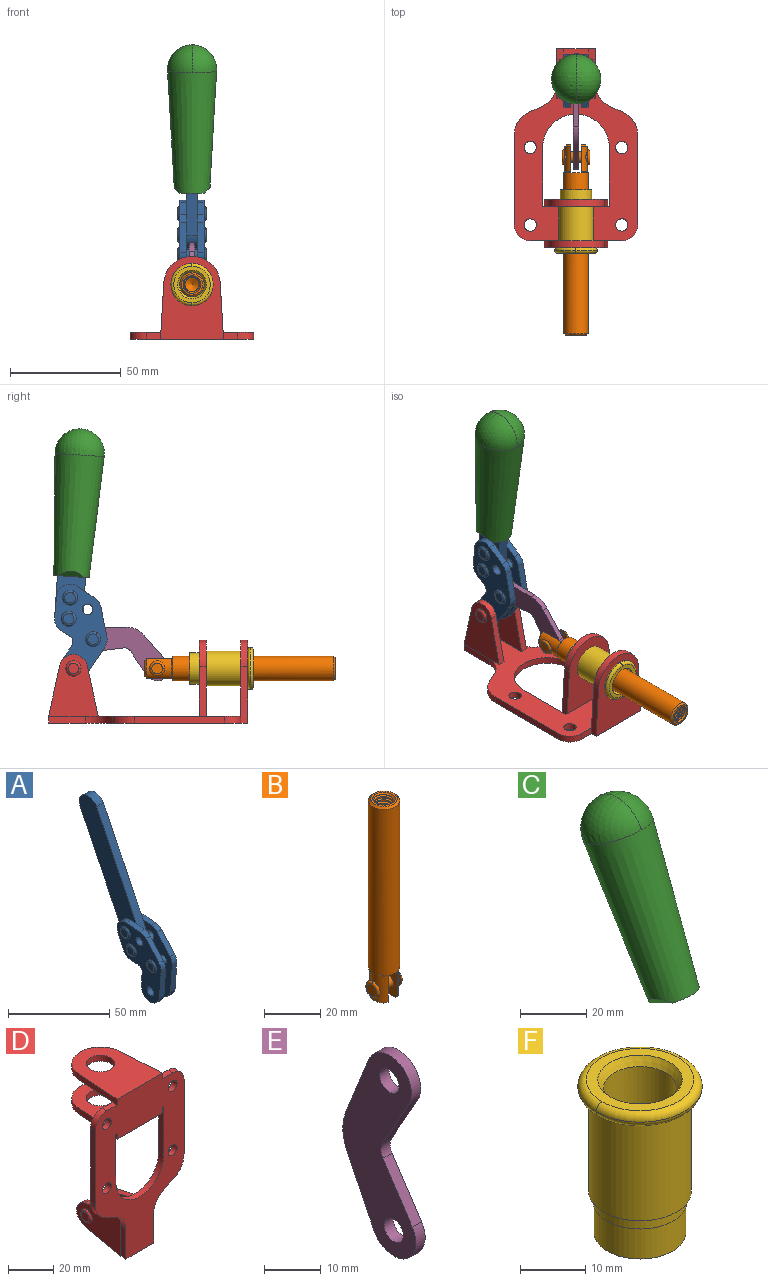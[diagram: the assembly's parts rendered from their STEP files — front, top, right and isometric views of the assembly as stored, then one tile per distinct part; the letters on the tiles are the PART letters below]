
ASSEMBLY  parts=6 mates=6
PART A: 59 faces, bbox 12.9x60.2x99.6 mm
  f0: torus R=2.39mm, axis (-1,0,0), area 14.9mm2, adj f20,f43,f51
  f1: torus R=2.39mm, axis (-1,0,0), area 14.9mm2, adj f19,f42,f51
  f2: torus R=2.39mm, axis (-1,0,0), area 14.9mm2, adj f18,f35,f51
  f3: torus R=2.39mm, axis (-1,0,0), area 14.9mm2, adj f14,f17,f23
  f4: torus R=2.39mm, axis (-1,0,0), area 14.9mm2, adj f13,f16,f23
  f5: torus R=2.39mm, axis (-1,0,0), area 14.9mm2, adj f12,f15,f23
  f6: cylinder r=2.39mm len=4.78mm, axis (1,0,0), area 46.5mm2, adj f48,f50,f51
  f7: cylinder r=2.39mm len=4.78mm, axis (1,0,0), area 46.5mm2, adj f50,f51
  f8: cylinder r=6.35mm len=12.68mm, axis (1,0,0), area 61.8mm2, adj f38,f39,f50,f51
  f9: cylinder r=2.39mm len=4.78mm, axis (-1,0,0), area 70.5mm2, adj f46,f50
  f10: cylinder r=2.39mm len=4.78mm, axis (-1,0,0), area 46.5mm2, adj f23,f45,f46
  f11: cylinder r=2.39mm len=4.78mm, axis (-1,0,0), area 46.5mm2, adj f23,f46
  f12: plane 4.78x4.78mm, normal (1,0,0), area 17.9mm2, adj f5,f15
  f13: plane 4.78x4.78mm, normal (1,0,0), area 17.9mm2, adj f4,f16
  f14: plane 4.78x4.78mm, normal (1,0,0), area 17.9mm2, adj f3,f17
  f15: torus R=2.39mm, axis (-1,0,0), area 14.9mm2, adj f5,f12,f23
  f16: torus R=2.39mm, axis (-1,0,0), area 14.9mm2, adj f4,f13,f23
  f17: torus R=2.39mm, axis (-1,0,0), area 14.9mm2, adj f3,f14,f23
  f18: plane 4.78x4.78mm, normal (-1,0,0), area 17.9mm2, adj f2,f35
  f19: plane 4.78x4.78mm, normal (-1,0,0), area 17.9mm2, adj f1,f42
  f20: plane 4.78x4.78mm, normal (-1,0,0), area 17.9mm2, adj f0,f43
  f21: plane 2.26x0.2mm, normal (1,0,0), area 0.2mm2, adj f31,f44
  f22: plane 2.26x0.2mm, normal (-1,0,0), area 0.2mm2, adj f41,f44
  f23: plane 39.37x30.77mm, normal (1,0,0), area 565.5mm2, adj f3,f4,f5,f10,f11,f15,f16,f17
  f24: cylinder r=6.1mm len=4.15mm, axis (-1,0,0), area 14.7mm2, adj f23,f25,f32,f46
  f25: plane 10.25x9.01mm, normal (0,-0.75,0.66), area 42.3mm2, adj f23,f24,f26,f46
  f26: cylinder r=6.35mm len=4.64mm, axis (-1,0,0), area 15.6mm2, adj f23,f25,f27,f46
  f27: plane 15.84x3.1mm, normal (0,-1,-0.07), area 49.2mm2, adj f23,f26,f28,f46
  f28: cylinder r=6.35mm len=12.68mm, axis (-1,0,0), area 61.8mm2, adj f23,f27,f29,f46
  f29: plane 8.11x3.1mm, normal (0,1,0.07), area 25.2mm2, adj f23,f28,f30,f46
  f30: cylinder r=3.05mm len=3.25mm, axis (-1,0,0), area 14.8mm2, adj f23,f29,f31,f46
  f31: plane 5.99x3.1mm, normal (0,0.07,-1), area 18.6mm2, adj f21,f23,f30,f44,f46
  f32: plane 9.5x3.1mm, normal (0,-0.07,1), area 29.5mm2, adj f23,f24,f33,f46,f47
  f33: cylinder r=6.1mm len=8.63mm, axis (-1,0,0), area 39.1mm2, adj f23,f32,f34,f47
  f34: plane 8.65x3.96mm, normal (0,0.91,-0.42), area 29.5mm2, adj f23,f33,f44,f47
  f35: torus R=2.39mm, axis (-1,0,0), area 14.9mm2, adj f2,f18,f51
  f36: plane 10.25x9.01mm, normal (0,-0.75,0.66), area 42.3mm2, adj f37,f49,f50,f51
  f37: cylinder r=6.35mm len=4.64mm, axis (1,0,0), area 15.6mm2, adj f36,f38,f50,f51
  f38: plane 15.84x3.1mm, normal (0,-1,-0.07), area 49.2mm2, adj f8,f37,f50,f51
  f39: plane 8.11x3.1mm, normal (0,1,0.07), area 25.2mm2, adj f8,f40,f50,f51
  f40: cylinder r=3.05mm len=3.25mm, axis (1,0,0), area 14.8mm2, adj f39,f41,f50,f51
  f41: plane 5.99x3.1mm, normal (0,0.07,-1), area 18.6mm2, adj f22,f40,f44,f50,f51
  f42: torus R=2.39mm, axis (-1,0,0), area 14.9mm2, adj f1,f19,f51
  f43: torus R=2.39mm, axis (-1,0,0), area 14.9mm2, adj f0,f20,f51
  f44: cylinder r=6.35mm len=12.12mm, axis (-1,0,0), area 128.9mm2, adj f21,f22,f23,f31,f34,f41,f46,f47
  f45: plane 2.65x1.35mm, normal (1,0,0), area 1mm2, adj f10,f55
  f46: plane 39.08x20.42mm, normal (-1,0,0), area 412.5mm2, adj f9,f10,f11,f24,f25,f26,f27,f28
  f47: plane 77.62x39.82mm, normal (1,0,0), area 850mm2, adj f32,f33,f34,f44,f53,f54,f55
  f48: plane 2.65x1.35mm, normal (-1,0,0), area 1mm2, adj f6,f55
  f49: cylinder r=6.1mm len=4.15mm, axis (1,0,0), area 14.7mm2, adj f36,f50,f51,f56
  f50: plane 39.08x20.42mm, normal (1,0,0), area 412.5mm2, adj f6,f7,f8,f9,f36,f37,f38,f39
  f51: plane 39.37x30.77mm, normal (-1,0,0), area 565.5mm2, adj f0,f1,f2,f6,f7,f8,f35,f36
  f52: plane 8.65x3.96mm, normal (0,0.91,-0.42), area 29.5mm2, adj f44,f51,f57,f58
  f53: plane 68.49x33.4mm, normal (0,0.9,-0.44), area 358.1mm2, adj f44,f47,f54,f58
  f54: cylinder r=6.35mm len=12.06mm, axis (1,0,0), area 93.7mm2, adj f47,f53,f55,f58
  f55: plane 68.49x33.4mm, normal (0,-0.9,0.44), area 358.1mm2, adj f44,f45,f46,f47,f48,f50,f54,f58
  f56: plane 9.5x3.1mm, normal (0,-0.07,1), area 29.5mm2, adj f49,f50,f51,f57,f58
  f57: cylinder r=6.1mm len=8.63mm, axis (1,0,0), area 39.1mm2, adj f51,f52,f56,f58
  f58: plane 77.62x39.82mm, normal (-1,0,0), area 850mm2, adj f44,f52,f53,f54,f55,f56,f57
PART B: 48 faces, bbox 12.6x11.1x86.1 mm
  f0: torus R=2.41mm, axis (-1,0,0), area 15mm2, adj f30,f32,f34
  f1: torus R=2.41mm, axis (-1,0,0), area 15mm2, adj f29,f31,f33
  f2: cylinder r=5.54mm len=72.39mm, axis (0,0,1), area 2518.5mm2, adj f3,f4,f42,f43
  f3: cone r=5.54mm half-angle=45deg, axis (0,0,1), area 7.6mm2, adj f2,f5,f41
  f4: cone r=5.54mm half-angle=45deg, axis (0,0,-1), area 34.9mm2, adj f2,f39
  f5: cylinder r=5.08mm len=11.48mm, axis (0,0,1), area 108.3mm2, adj f3,f7,f8,f41
  f6: cylinder r=2.41mm len=4.83mm, axis (-1,0,0), area 71.2mm2, adj f40,f41
  f7: cylinder r=2.41mm len=4.83mm, axis (-1,0,0), area 7.6mm2, adj f5,f34
  f8: cone r=5.08mm half-angle=45deg, axis (0,0,1), area 10.6mm2, adj f5,f37,f41
  f9: cone r=3.98mm half-angle=45deg, axis (0,0,1), area 17.6mm2, adj f27,f39,f45,f46,f47
  f10: cylinder r=2.41mm len=4.83mm, axis (-1,0,0), area 7.6mm2, adj f33,f38
  f11: cylinder r=3.2mm len=6.4mm, axis (0,0,1), area 78.4mm2, adj f12,f28,f44,f45,f47
  f12: cylinder r=3.2mm len=6.4mm, axis (0,0,1), area 10.5mm2, adj f11,f13,f45,f47
  f13: cylinder r=3.2mm len=6.4mm, axis (0,0,1), area 10.5mm2, adj f12,f14,f45,f47
  f14: cylinder r=3.2mm len=6.4mm, axis (0,0,1), area 10.5mm2, adj f13,f15,f45,f47
  f15: cylinder r=3.2mm len=6.4mm, axis (0,0,1), area 10.5mm2, adj f14,f16,f45,f47
  f16: cylinder r=3.2mm len=6.4mm, axis (0,0,1), area 10.5mm2, adj f15,f17,f45,f47
  f17: cylinder r=3.2mm len=6.4mm, axis (0,0,1), area 10.5mm2, adj f16,f18,f45,f47
  f18: cylinder r=3.2mm len=6.4mm, axis (0,0,1), area 10.5mm2, adj f17,f19,f45,f47
  f19: cylinder r=3.2mm len=6.4mm, axis (0,0,1), area 10.5mm2, adj f18,f20,f45,f47
  f20: cylinder r=3.2mm len=6.4mm, axis (0,0,1), area 10.5mm2, adj f19,f21,f45,f47
  f21: cylinder r=3.2mm len=6.4mm, axis (0,0,1), area 10.5mm2, adj f20,f22,f45,f47
  f22: cylinder r=3.2mm len=6.4mm, axis (0,0,1), area 10.5mm2, adj f21,f23,f45,f47
  f23: cylinder r=3.2mm len=6.4mm, axis (0,0,1), area 10.5mm2, adj f22,f24,f45,f47
  f24: cylinder r=3.2mm len=6.4mm, axis (0,0,1), area 10.5mm2, adj f23,f25,f45,f47
  f25: cylinder r=3.2mm len=6.4mm, axis (0,0,1), area 10.5mm2, adj f24,f26,f45,f47
  f26: cylinder r=3.2mm len=6.4mm, axis (0,0,1), area 10.5mm2, adj f25,f27,f45,f47
  f27: cylinder r=3.2mm len=6.4mm, axis (0,0,1), area 7.4mm2, adj f9,f26,f45,f47
  f28: cone r=3.2mm half-angle=60deg, axis (0,0,1), area 37.2mm2, adj f11
  f29: plane 4.83x4.83mm, normal (-1,0,0), area 18.3mm2, adj f1,f31
  f30: plane 4.83x4.83mm, normal (1,0,0), area 18.3mm2, adj f0,f32
  f31: torus R=2.41mm, axis (-1,0,0), area 15mm2, adj f1,f29,f33
  f32: torus R=2.41mm, axis (-1,0,0), area 15mm2, adj f0,f30,f34
  f33: plane 6.83x6.83mm, normal (1,0,0), area 18.3mm2, adj f1,f10,f31
  f34: plane 6.83x6.83mm, normal (-1,0,0), area 18.3mm2, adj f0,f7,f32
  f35: cone r=5.08mm half-angle=45deg, axis (0,0,1), area 10.6mm2, adj f36,f38,f40
  f36: plane 7.25x1.97mm, normal (0,0,-1), area 10mm2, adj f35,f40
  f37: plane 7.25x1.97mm, normal (0,0,-1), area 10mm2, adj f8,f41
  f38: cylinder r=5.08mm len=11.48mm, axis (0,0,1), area 108.3mm2, adj f10,f35,f40,f42
  f39: plane 9.55x9.55mm, normal (0,0,1), area 22mm2, adj f4,f9
  f40: plane 12.76x10.09mm, normal (1,0,0), area 95.7mm2, adj f6,f35,f36,f38,f42,f43
  f41: plane 12.76x10.09mm, normal (-1,0,0), area 95.7mm2, adj f3,f5,f6,f8,f37,f43
  f42: cone r=5.54mm half-angle=45deg, axis (0,0,1), area 7.6mm2, adj f2,f38,f40
  f43: plane 11.07x4.7mm, normal (0,0,-1), area 50.4mm2, adj f2,f40,f41
  f44: plane 0.89x0.62mm, normal (-1,0,0), area 0.3mm2, adj f11,f45,f46,f47
  f45: bspline ~24.8x7.63mm, area 266.6mm2, adj f9,f11,f12,f13,f14,f15,f16,f17
  f46: bspline ~24.87x7.63mm, area 73.6mm2, adj f9,f44,f45,f47
  f47: bspline ~24.98x7.63mm, area 272.5mm2, adj f9,f11,f12,f13,f14,f15,f16,f17
PART C: 11 faces, bbox 22.3x42.6x64.5 mm
  f0: sphere r=11.13mm, area 411.4mm2, adj f1,f8
  f1: cone r=11.11mm half-angle=3.3deg, axis (0,0.44,0.9), area 3251.8mm2, adj f0,f7,f8,f9,f10
  f2: cylinder r=6.16mm len=11.7mm, axis (1,0,0), area 89.5mm2, adj f3,f4,f5,f6
  f3: plane 60.23x36.75mm, normal (-1,0,0), area 763.6mm2, adj f2,f4,f6,f10
  f4: plane 51.37x25.05mm, normal (0,0.9,-0.44), area 264.2mm2, adj f2,f3,f5,f10
  f5: plane 60.23x36.75mm, normal (1,0,0), area 763.6mm2, adj f2,f4,f6,f10
  f6: plane 51.37x25.05mm, normal (0,-0.9,0.44), area 264.2mm2, adj f2,f3,f5,f10
  f7: plane 9.95x5.95mm, normal (0.71,-0.31,-0.64), area 25.8mm2, adj f1,f10
  f8: sphere r=11.13mm, area 411.4mm2, adj f0,f1
  f9: plane 9.95x5.95mm, normal (-0.71,-0.31,-0.64), area 25.8mm2, adj f1,f10
  f10: plane 14.27x11.38mm, normal (0,-0.44,-0.9), area 106.7mm2, adj f1,f3,f4,f5,f6,f7,f9
PART D: 55 faces, bbox 55.7x37.4x89.8 mm
  f0: torus R=2.41mm, axis (-1,0,0), area 15mm2, adj f11,f15,f25
  f1: torus R=2.41mm, axis (-1,0,0), area 15mm2, adj f10,f12,f22
  f2: cylinder r=2.78mm len=5.56mm, axis (0,-1,0), area 54.2mm2, adj f30,f54
  f3: cylinder r=14.99mm len=29.97mm, axis (0,-1,0), area 145.9mm2, adj f30,f49,f53,f54
  f4: cylinder r=2.78mm len=5.56mm, axis (0,-1,0), area 54.2mm2, adj f30,f54
  f5: cylinder r=2.78mm len=5.56mm, axis (0,-1,0), area 54.2mm2, adj f30,f54
  f6: cylinder r=2.78mm len=5.56mm, axis (0,-1,0), area 54.2mm2, adj f30,f54
  f7: cylinder r=6.35mm len=12.7mm, axis (0,0,1), area 123.6mm2, adj f27,f51
  f8: cylinder r=6.35mm len=12.7mm, axis (0,0,-1), area 124.7mm2, adj f21,f35
  f9: cylinder r=2.41mm len=11.18mm, axis (-1,0,0), area 169.4mm2, adj f16,f19
  f10: plane 4.83x4.83mm, normal (1,0,0), area 18.3mm2, adj f1,f12
  f11: plane 4.83x4.83mm, normal (-1,0,0), area 18.3mm2, adj f0,f15
  f12: torus R=2.41mm, axis (-1,0,0), area 15mm2, adj f1,f10,f22
  f13: cylinder r=6.35mm len=12.41mm, axis (1,0,0), area 53.4mm2, adj f18,f19,f22,f23
  f14: cylinder r=6.35mm len=12.41mm, axis (-1,0,0), area 53.4mm2, adj f16,f17,f24,f25
  f15: torus R=2.41mm, axis (-1,0,0), area 15mm2, adj f0,f11,f25
  f16: plane 27.86x22.35mm, normal (1,0,0), area 425.4mm2, adj f9,f14,f17,f24,f30
  f17: plane 22.86x4.97mm, normal (0,0.21,0.98), area 72.5mm2, adj f14,f16,f25,f30
  f18: plane 22.86x4.97mm, normal (0,0.21,0.98), area 72.5mm2, adj f13,f19,f22,f30
  f19: plane 27.86x22.35mm, normal (-1,0,0), area 425.4mm2, adj f9,f13,f18,f23,f30
  f20: cylinder r=12.7mm len=25.35mm, axis (0,0,-1), area 119.8mm2, adj f21,f34,f35,f36
  f21: plane 34.21x28.07mm, normal (0,0,-1), area 702.4mm2, adj f8,f20,f30,f34,f36
  f22: plane 27.96x22.45mm, normal (1,0,0), area 407.2mm2, adj f1,f12,f13,f18,f23,f30,f42,f43
  f23: plane 22.86x4.97mm, normal (0,0.21,-0.98), area 72.5mm2, adj f13,f19,f22,f44
  f24: plane 22.86x4.97mm, normal (0,0.21,-0.98), area 72.5mm2, adj f14,f16,f25,f44
  f25: plane 27.86x22.35mm, normal (-1,0,0), area 407.1mm2, adj f0,f14,f15,f17,f24,f30,f45,f46
  f26: plane 3.1x0.95mm, normal (0,0,-1), area 2.7mm2, adj f30,f49,f50,f54
  f27: plane 34.21x28.07mm, normal (0,0,1), area 702.4mm2, adj f7,f28,f30,f50,f52
  f28: cylinder r=12.7mm len=25.35mm, axis (0,0,1), area 118.8mm2, adj f27,f50,f51,f52
  f29: plane 3.1x0.95mm, normal (0,0,-1), area 2.7mm2, adj f30,f52,f53,f54
  f30: plane 86.54x55.63mm, normal (0,1,0), area 2362.9mm2, adj f2,f3,f4,f5,f6,f16,f17,f18
  f31: plane 40.56x3.1mm, normal (-1,0,0), area 125.7mm2, adj f30,f32,f48,f54
  f32: cylinder r=7.11mm len=7.11mm, axis (0,-1,0), area 34.6mm2, adj f30,f31,f33,f54
  f33: plane 6.67x3.1mm, normal (0,0,1), area 20.4mm2, adj f30,f32,f34,f54
  f34: plane 25.39x3.13mm, normal (-1,0.06,0), area 79.5mm2, adj f20,f21,f33,f35,f54
  f35: plane 37.31x28.45mm, normal (0,0,1), area 789.9mm2, adj f8,f20,f34,f36,f54
  f36: plane 25.39x3.13mm, normal (1,0.06,0), area 79.5mm2, adj f20,f21,f35,f37,f54
  f37: plane 6.67x3.1mm, normal (0,0,1), area 20.4mm2, adj f30,f36,f38,f54
  f38: cylinder r=7.11mm len=7.11mm, axis (0,-1,0), area 34.6mm2, adj f30,f37,f39,f54
  f39: plane 40.56x3.1mm, normal (1,0,0), area 125.7mm2, adj f30,f38,f40,f54
  f40: cylinder r=11.18mm len=10.16mm, axis (0,-1,0), area 39.5mm2, adj f30,f39,f41,f54
  f41: plane 6.09x3.1mm, normal (0.42,0,-0.91), area 20.8mm2, adj f30,f40,f42,f54
  f42: cylinder r=11.18mm len=9.41mm, axis (0,-1,0), area 37.2mm2, adj f22,f30,f41,f43,f54
  f43: plane 16.5x3.1mm, normal (1,0,0), area 51.1mm2, adj f22,f42,f44,f54
  f44: plane 17.37x3.1mm, normal (0,0,-1), area 53.8mm2, adj f23,f24,f30,f43,f45,f54
  f45: plane 16.5x3.1mm, normal (-1,0,0), area 51.1mm2, adj f25,f44,f46,f54
  f46: cylinder r=11.18mm len=9.41mm, axis (0,-1,0), area 37.2mm2, adj f25,f30,f45,f47,f54
  f47: plane 6.09x3.1mm, normal (-0.42,0,-0.91), area 20.8mm2, adj f30,f46,f48,f54
  f48: cylinder r=11.18mm len=10.16mm, axis (0,-1,0), area 39.5mm2, adj f30,f31,f47,f54
  f49: plane 26.54x3.1mm, normal (-1,0,0), area 82.3mm2, adj f3,f26,f30,f54
  f50: plane 25.39x3.1mm, normal (1,0.06,0), area 78.8mm2, adj f26,f27,f28,f51,f54
  f51: plane 37.31x28.45mm, normal (0,0,-1), area 789.9mm2, adj f7,f28,f50,f52,f54
  f52: plane 25.39x3.1mm, normal (-1,0.06,0), area 78.8mm2, adj f27,f28,f29,f51,f54
  f53: plane 26.54x3.1mm, normal (1,0,0), area 82.3mm2, adj f3,f29,f30,f54
  f54: plane 89.66x55.63mm, normal (0,-1,0), area 2678.5mm2, adj f2,f3,f4,f5,f6,f26,f29,f31
PART E: 12 faces, bbox 2.3x18.2x42.8 mm
  f0: cylinder r=2.4mm len=4.8mm, axis (1,0,0), area 34.9mm2, adj f4,f11
  f1: cylinder r=10.41mm len=8.47mm, axis (1,0,0), area 20.2mm2, adj f4,f9,f10,f11
  f2: cylinder r=3.05mm len=3.16mm, axis (1,0,0), area 7.7mm2, adj f4,f6,f7,f11
  f3: cylinder r=2.4mm len=4.8mm, axis (1,0,0), area 34.9mm2, adj f4,f11
  f4: plane 42.81x18.23mm, normal (-1,0,0), area 414.1mm2, adj f0,f1,f2,f3,f5,f6,f7,f8
  f5: cylinder r=5.54mm len=10.67mm, axis (1,0,0), area 41.8mm2, adj f4,f6,f10,f11
  f6: plane 11.66x6.53mm, normal (0,-0.87,-0.49), area 30.9mm2, adj f2,f4,f5,f11
  f7: plane 11.17x7.33mm, normal (0,-0.84,0.55), area 30.9mm2, adj f2,f4,f8,f11
  f8: cylinder r=5.54mm len=10.51mm, axis (1,0,0), area 41.8mm2, adj f4,f7,f9,f11
  f9: plane 13.67x6.67mm, normal (0,0.9,-0.44), area 35.1mm2, adj f1,f4,f8,f11
  f10: plane 14.1x5.7mm, normal (0,0.93,0.37), area 35.1mm2, adj f1,f4,f5,f11
  f11: plane 42.81x18.23mm, normal (1,0,0), area 414.1mm2, adj f0,f1,f2,f3,f5,f6,f7,f8
PART F: 15 faces, bbox 20.6x20.6x28.7 mm
  f0: torus R=8.26mm, axis (0,0,1), area 56.8mm2, adj f1,f10,f12
  f1: torus R=8.26mm, axis (0,0,1), area 56.8mm2, adj f0,f6,f13
  f2: cylinder r=5.59mm len=25.91mm, axis (0,0,1), area 909.6mm2, adj f3,f4
  f3: cone r=6.86mm half-angle=45deg, axis (0,0,-1), area 70.2mm2, adj f2,f14
  f4: cone r=6.47mm half-angle=30deg, axis (0,0,1), area 66.7mm2, adj f2,f13
  f5: cylinder r=7.04mm len=14.07mm, axis (0,0,1), area 252.6mm2, adj f11,f14
  f6: torus R=8.26mm, axis (0,0,1), area 56.8mm2, adj f1,f12,f13
  f7: cylinder r=7.16mm len=14.33mm, axis (0,0,1), area 91.5mm2, adj f9,f11
  f8: cylinder r=7.86mm len=18.42mm, axis (0,0,1), area 909.6mm2, adj f9,f10
  f9: plane 15.72x15.72mm, normal (0,0,-1), area 33mm2, adj f7,f8
  f10: plane 16.51x16.51mm, normal (0,0,-1), area 19.9mm2, adj f0,f8,f12
  f11: plane 14.33x14.33mm, normal (0,0,-1), area 5.7mm2, adj f5,f7
  f12: torus R=8.26mm, axis (0,0,1), area 56.8mm2, adj f0,f6,f10
  f13: plane 16.51x16.51mm, normal (0,0,1), area 82.7mm2, adj f1,f4,f6
  f14: plane 14.07x14.07mm, normal (0,0,-1), area 7.8mm2, adj f3,f5
PLACE A rot(axis=(1,0,0),29.8deg) t=(0,3.92,40.21)mm
PLACE B rot(axis=(1,0,0),90deg) t=(0,18.99,0)mm
PLACE C rot(axis=(1,0,0),29.8deg) t=(0.04,3.92,40.21)mm
PLACE D rot(axis=(1,0,0),90deg) t=(0,9.14,0)mm fixed
PLACE E rot(axis=(1,0,0),116.5deg) t=(0,28.35,9.51)mm
PLACE F rot(axis=(0.58,0.58,-0.58),120deg) t=(-24.61,9.14,24.61)mm
MATE revolute E.f3 <-> A.f4  axis (1,0,0) through (0,32.4,37.8)mm
MATE fastened C.f2 <-> A.f54  axis (-1,0,0) through (2.35,38.3,123.06)mm
MATE fastened F.f2 <-> B.f2  axis (0,-1,0) through (0,-39.79,24.61)mm
MATE revolute E.f5 <-> B.f6  axis (1,0,0) through (0,3.51,24.61)mm
MATE fastened F.f2 <-> D.f7  axis (0,1,0) through (0,-37.25,24.61)mm
MATE revolute A.f7 <-> D.f0  axis (1,0,0) through (0,41.23,24.61)mm
